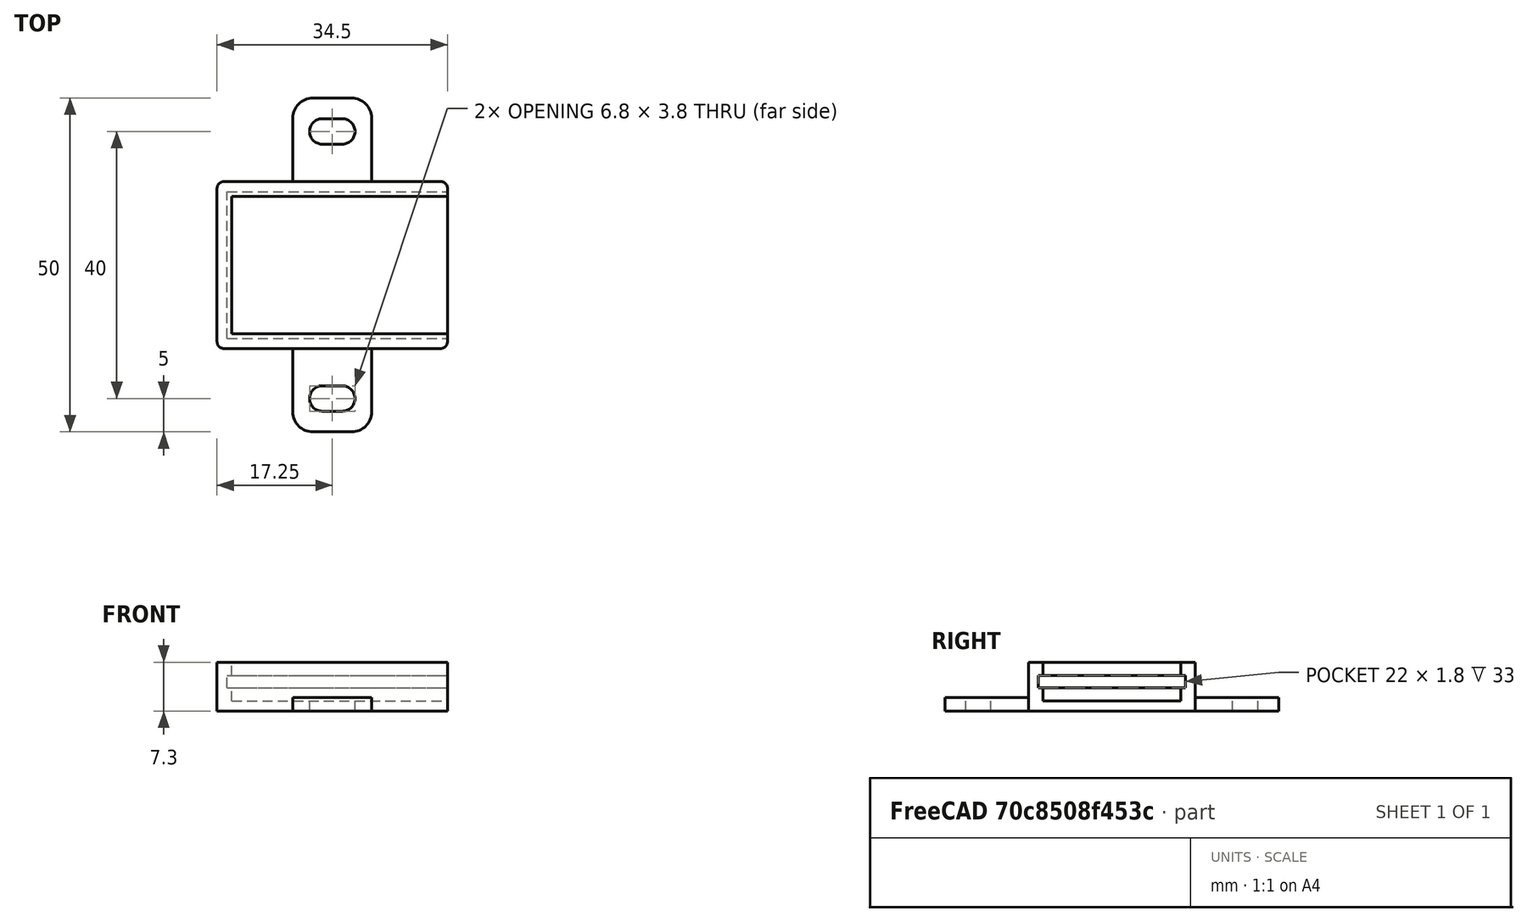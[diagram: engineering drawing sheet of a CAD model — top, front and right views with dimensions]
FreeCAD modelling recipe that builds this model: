
FCSTD DOCUMENT  (FreeCAD 0.19R)
Label: leds_32x22_5_led_plus_common
License: FreeArt
LicenseURL: http://artlibre.org/licence/lal
objects: Part::Box×3, Part::MultiFuse×2, Spreadsheet::Sheet×1, Part::Fillet×1, Part::Feature×1, Part::Cut×1, App::Part×1
note: 8 computed .brp shape members not serialized (recipe doc carries the construction recipe); baked Part::Feature solids carry a one-line shape summary decoded from their .brp

FEATURE [Spreadsheet::Sheet] Spreadsheet  label="p"
  cells = A1=pcb_x; B1(pcb_x)=33; A2=pcb_y; B2(pcb_y)=22; A3=pcb_z; B3(pcb_z)=1.8; A4=pcb_under; B4(pcb_under)=2; A5=side_wall; B5(side_wall)=1.5; A6=pcb_side_lane; B6(pcb_side_lane)=0.7; A7=bottom_wall; B7(bottom_wall)=1.5; A8=pcb_above; B8(pcb_above)=2
FEATURE [Part::Box] Box  label="external cube"
  AttacherType = Attacher::AttachEngine3D
  Height = 7.3
  Length = 34.5
  Width = 25
  expr: Length = <<p>>.pcb_x + <<p>>.side_wall
  expr: Width = <<p>>.pcb_y + 2 * <<p>>.side_wall
  expr: Height = <<p>>.bottom_wall + <<p>>.pcb_under + <<p>>.pcb_z + <<p>>.pcb_above
FEATURE [Part::Box] Box006  label="internal cube"
  AttacherType = Attacher::AttachEngine3D
  Height = 5.8
  Length = 33.1
  Placement = pos=(2.2,2.2,1.5) rot=(0,0,1;0rad)
  Width = 20.6
  expr: Length = <<p>>.pcb_x - 2 * <<p>>.pcb_side_lane + <<p>>.side_wall
  expr: Width = <<p>>.pcb_y - 2 * <<p>>.pcb_side_lane
  expr: Height = <<p>>.pcb_under + <<p>>.pcb_z + <<p>>.pcb_above
  expr: .Placement.Base.z = <<p>>.bottom_wall
  expr: .Placement.Base.x = <<p>>.side_wall + <<p>>.pcb_side_lane
  expr: .Placement.Base.y = <<p>>.side_wall + <<p>>.pcb_side_lane
FEATURE [Part::Box] Box007  label="pcb extract cube"
  AttacherType = Attacher::AttachEngine3D
  Height = 1.8
  Length = 33
  Placement = pos=(1.5,1.5,3.5) rot=(0,0,1;0rad)
  Width = 22
  expr: Height = <<p>>.pcb_z
  expr: .Placement.Base.z = <<p>>.bottom_wall + <<p>>.pcb_under
  expr: Width = <<p>>.pcb_y
  expr: Length = <<p>>.pcb_x
  expr: .Placement.Base.x = <<p>>.side_wall
  expr: .Placement.Base.y = <<p>>.side_wall
FEATURE [Part::MultiFuse] Fusion  label="extract fusion"
  Shapes = -> [Box006,Box007]
FEATURE [Part::Fillet] Fillet  label="external fillet"
  Base = -> Box
  Edges = 4 edges r=1: [Edge1,Edge3,Edge5,Edge7]
FEATURE [Part::Feature] Cut002001  label="attach plane y dir001"
  Placement = pos=(11.35,-12.5,0) rot=(0,0,1;0rad)
  shape: bbox 11.8 x 50 x 2 mm, 20 faces (baked)
FEATURE [Part::MultiFuse] Fusion001  label="solid fusion"
  Shapes = -> [Fillet,Cut002001]
FEATURE [Part::Cut] Cut  label="body cut"
  Base = -> Fusion001
  Tool = -> Fusion
FEATURE [App::Part] Part  label="leds_8_gnd_common part"
  Group = -> [Box,Fillet,Fusion001,Fusion,Box007,Box006,Cut]
  Origin = -> Origin
